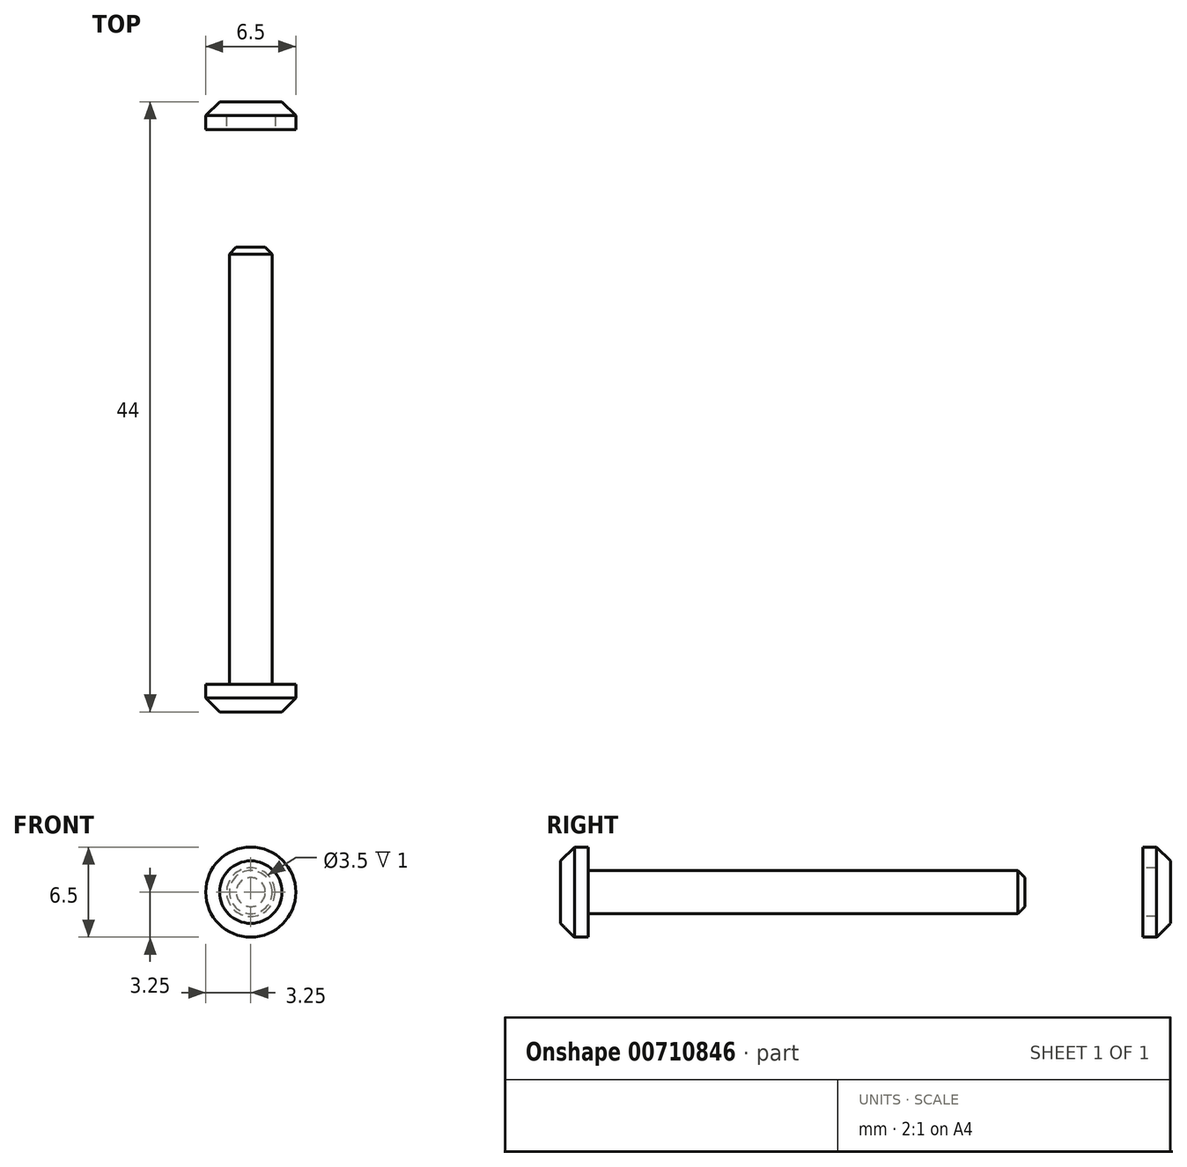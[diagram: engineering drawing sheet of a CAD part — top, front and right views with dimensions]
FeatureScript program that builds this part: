
annotation { "Feature Type Name" : "Feature", "Feature Type Description" : "" }
export const myFeature = defineFeature(function(context is Context, id is Id, definition is map)
    precondition{}
    {
        {
            var Q0;
            Q0=qCreatedBy(makeId("Front.planeOp"),FACE);
            var sketch = newSketch(context, id + "F0", { "sketchPlane" : qUnion([Q0])});
            skCircle(sketch, "E0", {"center": v(0, 0) * mm, "radius": 1.75 * mm});
            skCircle(sketch, "E1", {"center": v(0, 0) * mm, "radius": 3.25 * mm});
            skCircle(sketch, "E2.0", {"center": v(0, 0) * mm, "radius": 1.55 * mm});
            skSolve(sketch);
        }
        {
            var Q0;
            Q0=makeQuery(id+"F0.imprint","IMPRINT",FACE,{"disambiguationData":[TD([[makeQuery(id+"F0.imprint","IMPRINT",EDGE,{"derivedFrom":sQuery(id+"F0.wireOp",EDGE,"E2.0")}),1.0]])]});
            extrude(context, id + "F1", {"entities" : qUnion([Q0]), "oppositeDirection" : true, "depth" : 31.5 * mm, "offsetDistance" : 25 * mm});
        }
        {
            var Q0;
            Q0=makeQuery(id+"F0.imprint","IMPRINT",FACE,{"disambiguationData":[TD([[makeQuery(id+"F0.imprint","IMPRINT",EDGE,{"derivedFrom":sQuery(id+"F0.wireOp",EDGE,"E0")}),-1.0]])]});
            var Q1;
            Q1=makeQuery(id+"F0.imprint","IMPRINT",FACE,{"disambiguationData":[TD([[makeQuery(id+"F0.imprint","IMPRINT",EDGE,{"derivedFrom":sQuery(id+"F0.wireOp",EDGE,"E0")}),1.0]])]});
            var Q2;
            Q2=makeQuery(id+"F0.imprint","IMPRINT",FACE,{"disambiguationData":[TD([[makeQuery(id+"F0.imprint","IMPRINT",EDGE,{"derivedFrom":sQuery(id+"F0.wireOp",EDGE,"E2.0")}),1.0]])]});
            extrude(context, id + "F2", {"entities" : qUnion([Q0, Q1, Q2]), "operationType" : NewBodyOperationType.ADD, "depth" : 2 * mm, "offsetDistance" : 25 * mm});
        }
        {
            var Q0;
            Q0=makeQuery(id+"F2.opExtrude","CAP_EDGE",EDGE,{"disambiguationData":[OSD([sQuery(id+"F0.wireOp",EDGE,"E1")])],"isStart":false});
            chamfer(context, id + "F3", {"entities" : qUnion([Q0]), "width" : 1 * mm, "tangentPropagation" : true});
        }
        {
            var Q0;
            Q0=makeQuery(id+"F1.opExtrude","CAP_EDGE",EDGE,{"disambiguationData":[OSD([sQuery(id+"F0.wireOp",EDGE,"E2.0")])],"isStart":false});
            chamfer(context, id + "F4", {"entities" : qUnion([Q0]), "width" : .5 * mm, "tangentPropagation" : true});
        }
        {
            var Q0;
            Q0=makeQuery(id+"F0.imprint","IMPRINT",FACE,{"disambiguationData":[TD([[makeQuery(id+"F0.imprint","IMPRINT",EDGE,{"derivedFrom":sQuery(id+"F0.wireOp",EDGE,"E0")}),-1.0]])]});
            extrude(context, id + "F5", {"entities" : qUnion([Q0]), "oppositeDirection" : true, "depth" : 42 * mm, "offsetDistance" : 25 * mm, "hasSecondDirection" : true, "secondDirectionOppositeDirection" : true, "secondDirectionDepth" : 40 * mm});
        }
        {
            var Q0;
            Q0=makeQuery(id+"F0.imprint","IMPRINT",FACE,{"disambiguationData":[TD([[makeQuery(id+"F0.imprint","IMPRINT",EDGE,{"derivedFrom":sQuery(id+"F0.wireOp",EDGE,"E0")}),1.0]])]});
            var Q1;
            Q1=makeQuery(id+"F0.imprint","IMPRINT",FACE,{"disambiguationData":[TD([[makeQuery(id+"F0.imprint","IMPRINT",EDGE,{"derivedFrom":sQuery(id+"F0.wireOp",EDGE,"E2.0")}),1.0]])]});
            extrude(context, id + "F6", {"entities" : qUnion([Q0, Q1]), "operationType" : NewBodyOperationType.ADD, "oppositeDirection" : true, "depth" : 42 * mm, "offsetDistance" : 25 * mm, "hasSecondDirection" : true, "secondDirectionOppositeDirection" : true, "secondDirectionDepth" : 41 * mm});
        }
        {
            var Q0;
            Q0=makeQuery(id+"F5.opExtrude","CAP_EDGE",EDGE,{"disambiguationData":[OSD([sQuery(id+"F0.wireOp",EDGE,"E1")])],"isStart":false});
            chamfer(context, id + "F7", {"entities" : qUnion([Q0]), "width" : 1 * mm, "tangentPropagation" : true});
        }
    });
